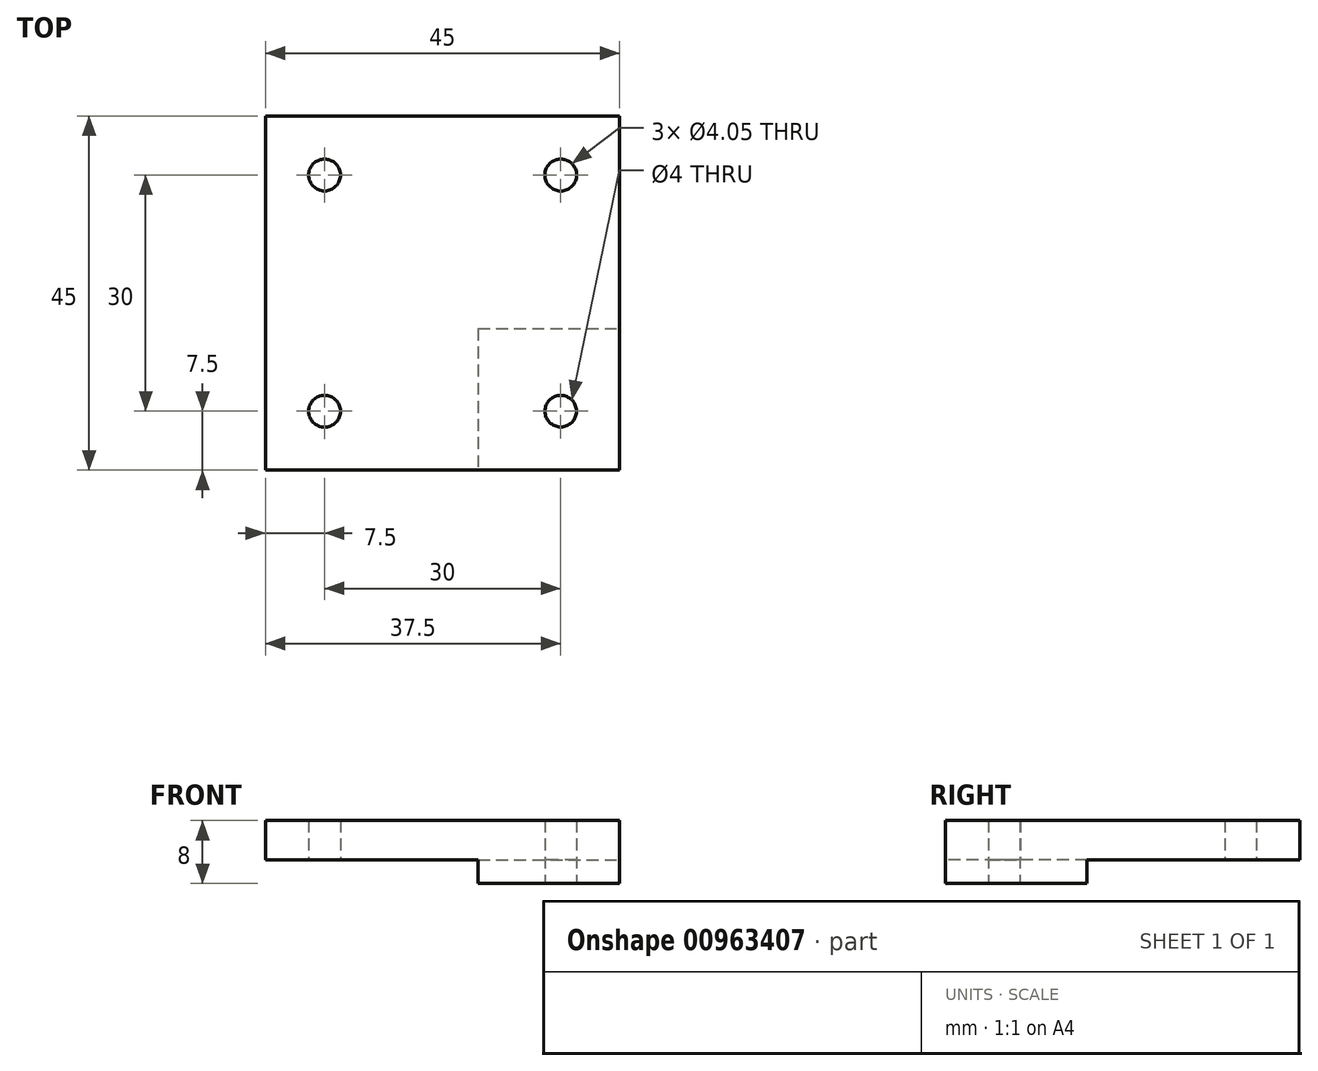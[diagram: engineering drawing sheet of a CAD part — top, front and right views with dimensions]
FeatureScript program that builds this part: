
annotation { "Feature Type Name" : "Feature", "Feature Type Description" : "" }
export const myFeature = defineFeature(function(context is Context, id is Id, definition is map)
    precondition{}
    {
        {
            var Q0;
            Q0=qCreatedBy(makeId("Top.planeOp"),FACE);
            var sketch = newSketch(context, id + "F0", { "sketchPlane" : qUnion([Q0])});
            skLineSegment(sketch, "E0", {"start": v(0, 0) * mm, "end": v(0, 15) * mm, "construction": true});
            skLineSegment(sketch, "E1", {"start": v(0, 0) * mm, "end": v(-15, 0) * mm, "construction": true});
            skLineSegment(sketch, "E2", {"start": v(-15, 0) * mm, "end": v(-15, 15) * mm, "construction": true});
            skLineSegment(sketch, "E3", {"start": v(-15, 15) * mm, "end": v(0, 15) * mm, "construction": true});
            skPoint(sketch, "E4.positionSnap0", {"position": v(-15, 7.5) * mm});
            skPoint(sketch, "E4.positionSnap1", {"position": v(-7.5, 0) * mm});
            skLineSegment(sketch, "E5", {"start": v(-15, 15) * mm, "end": v(-15, 0) * mm});
            skLineSegment(sketch, "E6", {"start": v(-15, 0) * mm, "end": v(0, 0) * mm});
            skLineSegment(sketch, "E7", {"start": v(-15, 15) * mm, "end": v(0, 15) * mm});
            skLineSegment(sketch, "E8", {"start": v(0, 15) * mm, "end": v(15, 15) * mm});
            skLineSegment(sketch, "E9", {"start": v(0, 0) * mm, "end": v(15, 0) * mm});
            skPoint(sketch, "E10.positionSnap0", {"position": v(7.5, 0) * mm});
            skPoint(sketch, "E10.positionSnap1", {"position": v(0, 7.5) * mm});
            skLineSegment(sketch, "E11", {"start": v(15, 15) * mm, "end": v(15, 0) * mm});
            skLineSegment(sketch, "E12.MirrorCS", {"start": v(-15, -15) * mm, "end": v(-15, 0) * mm});
            skLineSegment(sketch, "E13.MirrorCS", {"start": v(0, 0) * mm, "end": v(0, -15) * mm, "construction": true});
            skLineSegment(sketch, "E14.MirrorCS", {"start": v(-15, -15) * mm, "end": v(0, -15) * mm});
            skLineSegment(sketch, "E15", {"start": v(0, 0) * mm, "end": v(0, -15) * mm});
            skLineSegment(sketch, "E16", {"start": v(-3, -15) * mm, "end": v(-3, 0) * mm, "construction": true});
            skLineSegment(sketch, "E17.bottom", {"start": v(-3, 0) * mm, "end": v(0, 0) * mm, "construction": true});
            skLineSegment(sketch, "E17.top", {"start": v(-3, 3) * mm, "end": v(0, 3) * mm, "construction": true});
            skLineSegment(sketch, "E17.left", {"start": v(-3, 0) * mm, "end": v(-3, 3) * mm, "construction": true});
            skLineSegment(sketch, "E17.right", {"start": v(0, 0) * mm, "end": v(0, 3) * mm, "construction": true});
            skLineSegment(sketch, "E18", {"start": v(0, 3) * mm, "end": v(15, 3) * mm, "construction": true});
            skLineSegment(sketch, "E19", {"start": v(-3, 3) * mm, "end": v(15, 3) * mm});
            skLineSegment(sketch, "E20", {"start": v(-3, 3) * mm, "end": v(-3, -15) * mm});
            skLineSegment(sketch, "E21.bottom", {"start": v(-15, 15) * mm, "end": v(-30, 15) * mm});
            skLineSegment(sketch, "E21.top", {"start": v(-15, 0) * mm, "end": v(-30, 0) * mm});
            skLineSegment(sketch, "E21.right", {"start": v(-30, 15) * mm, "end": v(-30, 0) * mm});
            skLineSegment(sketch, "E22.MirrorCS", {"start": v(-30, -15) * mm, "end": v(-30, 0) * mm});
            skLineSegment(sketch, "E23.MirrorCS", {"start": v(-15, -15) * mm, "end": v(-30, -15) * mm});
            skLineSegment(sketch, "E24.MirrorCS", {"start": v(-15, 0) * mm, "end": v(-15, -15) * mm, "construction": true});
            skCircle(sketch, "E25.MirrorC", {"center": v(-22.5, -7.5) * mm, "radius": 2.02 * mm});
            skLineSegment(sketch, "E26.MirrorCS", {"start": v(-30, 15) * mm, "end": v(-30, 30) * mm});
            skLineSegment(sketch, "E27.MirrorCS", {"start": v(-15, 30) * mm, "end": v(-15, 15) * mm, "construction": true});
            skLineSegment(sketch, "E28.MirrorCS", {"start": v(-15, 30) * mm, "end": v(-30, 30) * mm});
            skLineSegment(sketch, "E29", {"start": v(-15, 30) * mm, "end": v(-15, 15) * mm});
            skLineSegment(sketch, "E30", {"start": v(-15, 30) * mm, "end": v(0, 30) * mm});
            skLineSegment(sketch, "E31", {"start": v(0, 30) * mm, "end": v(0, 15) * mm});
            skLineSegment(sketch, "E32", {"start": v(0, 30) * mm, "end": v(15, 30) * mm});
            skLineSegment(sketch, "E33", {"start": v(15, 30) * mm, "end": v(15, 15) * mm});
            skCircle(sketch, "E34.MirrorC", {"center": v(7.5, 22.5) * mm, "radius": 2.02 * mm});
            skPoint(sketch, "E35", {"position": v(-22.5, 22.5) * mm});
            skPoint(sketch, "E35.positionSnap0", {"position": v(-30, 22.5) * mm});
            skPoint(sketch, "E35.positionSnap1", {"position": v(-22.5, 15) * mm});
            skCircle(sketch, "E36", {"center": v(-22.5, 22.5) * mm, "radius": 2.02 * mm});
            skSolve(sketch);
        }
        {
            var Q0;
            Q0=makeQuery(id+"F0.imprint","IMPRINT",FACE,{"disambiguationData":[TD([[makeQuery(id+"F0.imprint","IMPRINT",EDGE,{"derivedFrom":sQuery(id+"F0.wireOp",EDGE,"E6")}),-1.0]])]});
            var Q1;
            Q1=makeQuery(id+"F0.imprint","IMPRINT",FACE,{"disambiguationData":[TD([[makeQuery(id+"F0.imprint","IMPRINT",EDGE,{"derivedFrom":sQuery(id+"F0.wireOp",EDGE,"D9yUUFfh-uHx8-PHrj-J6m0-1j0Mg3FFPIsq")}),-1.0]])]});
            var Q2;
            {var subQ1=sQuery(id+"F0.wireOp",EDGE,"E12.MirrorCS");Q2=makeQuery(id+"F0.imprint","IMPRINT",FACE,{"disambiguationData":[TD([[makeQuery(id+"F0.imprint","IMPRINT",EDGE,{"derivedFrom":subQ1}),-1.0]])]});}
            var Q3;
            {var subQ1=sQuery(id+"F0.wireOp",EDGE,"E9");Q3=makeQuery(id+"F0.imprint","IMPRINT",FACE,{"disambiguationData":[TD([[makeQuery(id+"F0.imprint","IMPRINT",EDGE,{"derivedFrom":subQ1}),1.0]])]});}
            extrude(context, id + "F1", {"entities" : qUnion([Q0, Q1, Q2, Q3]), "depth" : 5 * mm, "offsetDistance" : 25 * mm});
        }
        {
            var Q0;
            {var subQ0=sQuery(id+"F0.wireOp",EDGE,"E15");Q0=makeQuery(id+"F0.imprint","IMPRINT",FACE,{"disambiguationData":[TD([[makeQuery(id+"F0.imprint","IMPRINT",EDGE,{"derivedFrom":subQ0}),-1.0]])]});}
            var Q1;
            {var subQ1=sQuery(id+"F0.wireOp",EDGE,"E9");Q1=makeQuery(id+"F0.imprint","IMPRINT",FACE,{"disambiguationData":[TD([[makeQuery(id+"F0.imprint","IMPRINT",EDGE,{"derivedFrom":subQ1}),1.0]])]});}
            extrude(context, id + "F2", {"entities" : qUnion([Q0, Q1]), "operationType" : NewBodyOperationType.ADD, "oppositeDirection" : true, "depth" : 3 * mm, "offsetDistance" : 25 * mm});
        }
        {
            var Q0;
            Q0=makeQuery(id+"F2.opExtrude","CAP_FACE",FACE,{"disambiguationData":[OSD([sQuery(id+"F0.wireOp",EDGE,"E9"),sQuery(id+"F0.wireOp",EDGE,"E11"),sQuery(id+"F0.wireOp",EDGE,"E14.MirrorCS"),sQuery(id+"F0.wireOp",EDGE,"E15"),sQuery(id+"F0.wireOp",EDGE,"E19"),sQuery(id+"F0.wireOp",EDGE,"E20")])],"isStart":false});
            var sketch = newSketch(context, id + "F3", { "sketchPlane" : qUnion([Q0])});
            skLineSegment(sketch, "E37.bottom", {"start": v(0, 15) * mm, "end": v(15, 15) * mm});
            skLineSegment(sketch, "E37.top", {"start": v(0, 0) * mm, "end": v(15, 0) * mm});
            skLineSegment(sketch, "E37.left", {"start": v(0, 15) * mm, "end": v(0, 0) * mm});
            skLineSegment(sketch, "E37.right", {"start": v(15, 15) * mm, "end": v(15, 0) * mm});
            skCircle(sketch, "E38", {"center": v(7.5, 7.5) * mm, "radius": 2 * mm});
            skPoint(sketch, "E38.centerSnap0", {"position": v(7.5, 0) * mm});
            skPoint(sketch, "E38.centerSnap1", {"position": v(0, 7.5) * mm});
            skSolve(sketch);
        }
        {
            var Q0;
            Q0=makeQuery(id+"F3.imprint","IMPRINT",FACE,{"disambiguationData":[TD([[makeQuery(id+"F3.imprint","IMPRINT",EDGE,{"derivedFrom":sQuery(id+"F3.wireOp",EDGE,"E37.bottom")}),-1.0]])]});
            extrude(context, id + "F4", {"entities" : qUnion([Q0]), "operationType" : NewBodyOperationType.ADD, "oppositeDirection" : true, "depth" : 8 * mm, "offsetDistance" : 25 * mm});
        }
        {
            var Q0;
            Q0=makeQuery(id+"F0.imprint","IMPRINT",FACE,{"disambiguationData":[TD([[makeQuery(id+"F0.imprint","IMPRINT",EDGE,{"derivedFrom":sQuery(id+"F0.wireOp",EDGE,"E12.MirrorCS")}),1.0]])]});
            var Q1;
            Q1=makeQuery(id+"F0.imprint","IMPRINT",FACE,{"disambiguationData":[TD([[makeQuery(id+"F0.imprint","IMPRINT",EDGE,{"derivedFrom":sQuery(id+"F0.wireOp",EDGE,"E21.bottom")}),1.0]])]});
            var Q2;
            Q2=makeQuery(id+"F0.imprint","IMPRINT",FACE,{"disambiguationData":[TD([[makeQuery(id+"F0.imprint","IMPRINT",EDGE,{"derivedFrom":sQuery(id+"F0.wireOp",EDGE,"E7")}),-1.0]])]});
            var Q3;
            Q3=makeQuery(id+"F0.imprint","IMPRINT",FACE,{"disambiguationData":[TD([[makeQuery(id+"F0.imprint","IMPRINT",EDGE,{"derivedFrom":sQuery(id+"F0.wireOp",EDGE,"E7")}),1.0]])]});
            var Q4;
            Q4=makeQuery(id+"F0.imprint","IMPRINT",FACE,{"disambiguationData":[TD([[makeQuery(id+"F0.imprint","IMPRINT",EDGE,{"derivedFrom":sQuery(id+"F0.wireOp",EDGE,"E8")}),1.0]])]});
            var Q5;
            Q5=makeQuery(id+"F0.imprint","IMPRINT",FACE,{"disambiguationData":[TD([[makeQuery(id+"F0.imprint","IMPRINT",EDGE,{"derivedFrom":sQuery(id+"F0.wireOp",EDGE,"E21.bottom")}),-1.0]])]});
            extrude(context, id + "F5", {"entities" : qUnion([Q0, Q1, Q2, Q3, Q4, Q5]), "operationType" : NewBodyOperationType.ADD, "depth" : 5 * mm, "offsetDistance" : 25 * mm});
        }
    });
